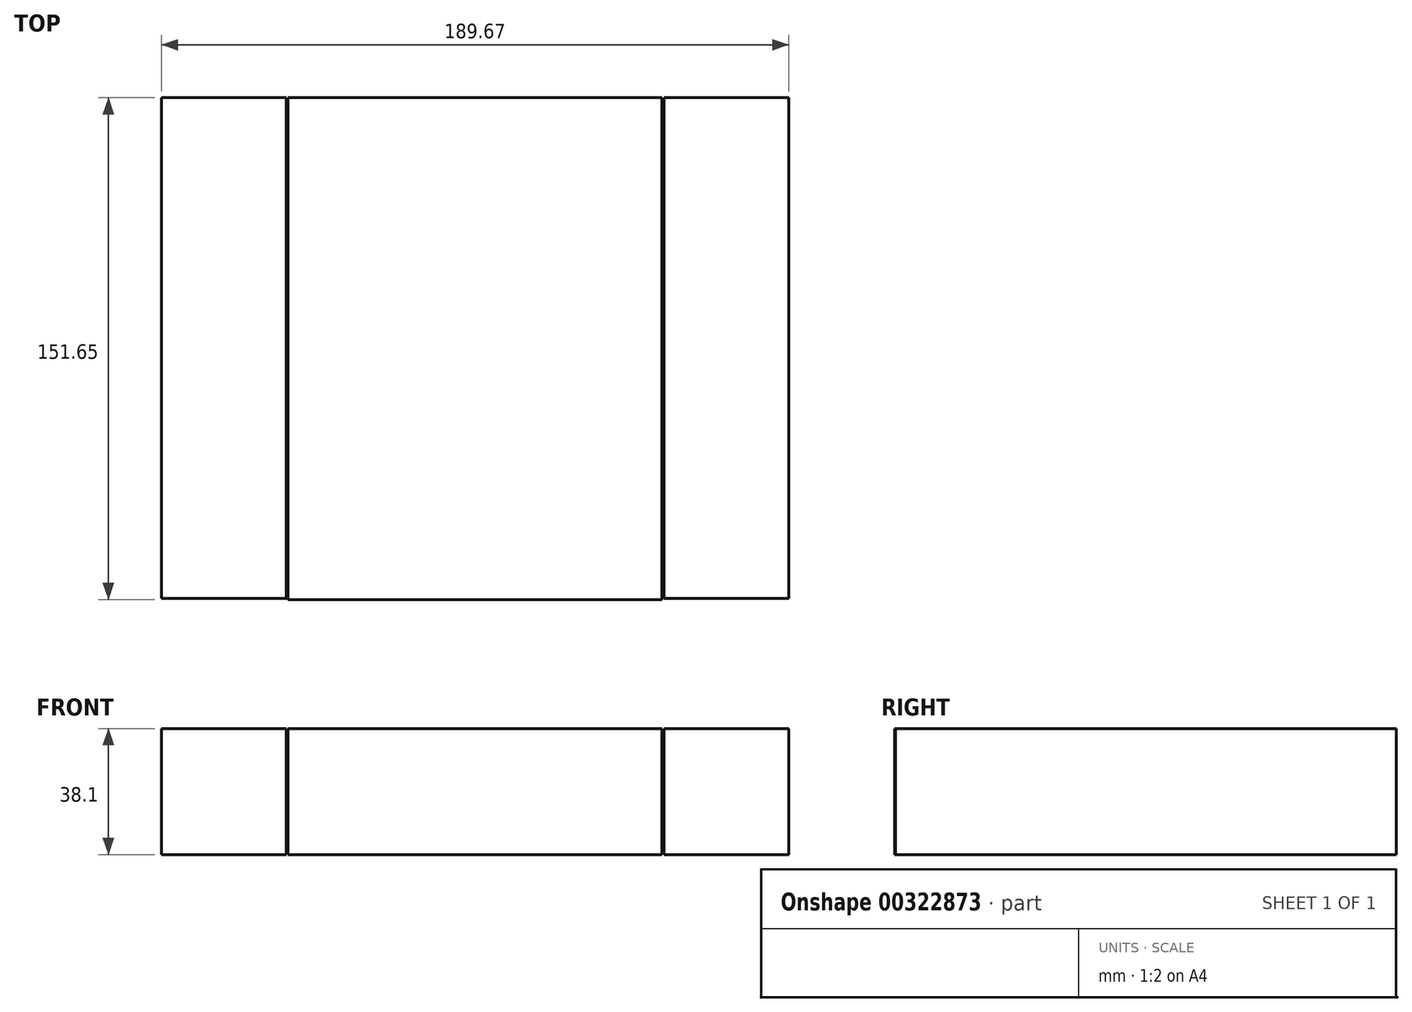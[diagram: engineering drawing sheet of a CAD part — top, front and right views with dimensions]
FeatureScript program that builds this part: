
annotation { "Feature Type Name" : "Feature", "Feature Type Description" : "" }
export const myFeature = defineFeature(function(context is Context, id is Id, definition is map)
    precondition{}
    {
        {
            var Q0;
            Q0=qCreatedBy(makeId("Top.planeOp"),FACE);
            var sketch = newSketch(context, id + "F0", { "sketchPlane" : qUnion([Q0])});
            skLineSegment(sketch, "E0.bottom", {"start": v(-75.56, 75.7) * mm, "end": v(37.5, 75.7) * mm});
            skLineSegment(sketch, "E0.top", {"start": v(-75.56, -75.96) * mm, "end": v(37.5, -75.96) * mm});
            skLineSegment(sketch, "E0.left", {"start": v(-75.56, 75.7) * mm, "end": v(-75.56, -75.96) * mm});
            skLineSegment(sketch, "E0.right", {"start": v(37.5, 75.7) * mm, "end": v(37.5, -75.96) * mm});
            skSolve(sketch);
        }
        {
            var Q0;
            Q0=makeQuery(id+"F0.imprint","IMPRINT",FACE,{"disambiguationData":[TD([[makeQuery(id+"F0.imprint","IMPRINT",EDGE,{"derivedFrom":sQuery(id+"F0.wireOp",EDGE,"E0.bottom")}),-1.0]])]});
            var Q1;
            Q1 = qSketchRegion(id + "F0", true);
            extrude(context, id + "F1", {"entities" : qUnion([Q0, Q1]), "depth" : 38.1 * mm});
        }
        {
            var Q0;
            Q0=qCreatedBy(makeId("Top.planeOp"),FACE);
            var sketch = newSketch(context, id + "F2", { "sketchPlane" : qUnion([Q0])});
            skLineSegment(sketch, "E1.bottom", {"start": v(38.05, 75.7) * mm, "end": v(75.83, 75.7) * mm});
            skLineSegment(sketch, "E1.top", {"start": v(38.05, -75.7) * mm, "end": v(75.83, -75.7) * mm});
            skLineSegment(sketch, "E1.left", {"start": v(38.05, 75.7) * mm, "end": v(38.05, -75.7) * mm});
            skLineSegment(sketch, "E1.right", {"start": v(75.83, 75.7) * mm, "end": v(75.83, -75.7) * mm});
            skSolve(sketch);
        }
        {
            var Q0;
            Q0 = qSketchRegion(id + "F2", true);
            extrude(context, id + "F3", {"entities" : qUnion([Q0]), "depth" : 38.1 * mm});
        }
        {
            var Q0;
            Q0=makeQuery(id+"F3.opExtrude","SWEPT_BODY",BODY,{"disambiguationData":[OSD([sQuery(id+"F2.wireOp",EDGE,"E1.bottom"),sQuery(id+"F2.wireOp",EDGE,"E1.top"),sQuery(id+"F2.wireOp",EDGE,"E1.left"),sQuery(id+"F2.wireOp",EDGE,"E1.right")])]});
            transform(context, id + "F4", {"entities" : qUnion([Q0]), "transformType" : TransformType.TRANSLATION_3D, "dx" : -151.9 * mm, "dy" : 0 * mm, "dz" : 0 * mm, "makeCopy" : true});
        }
    });
